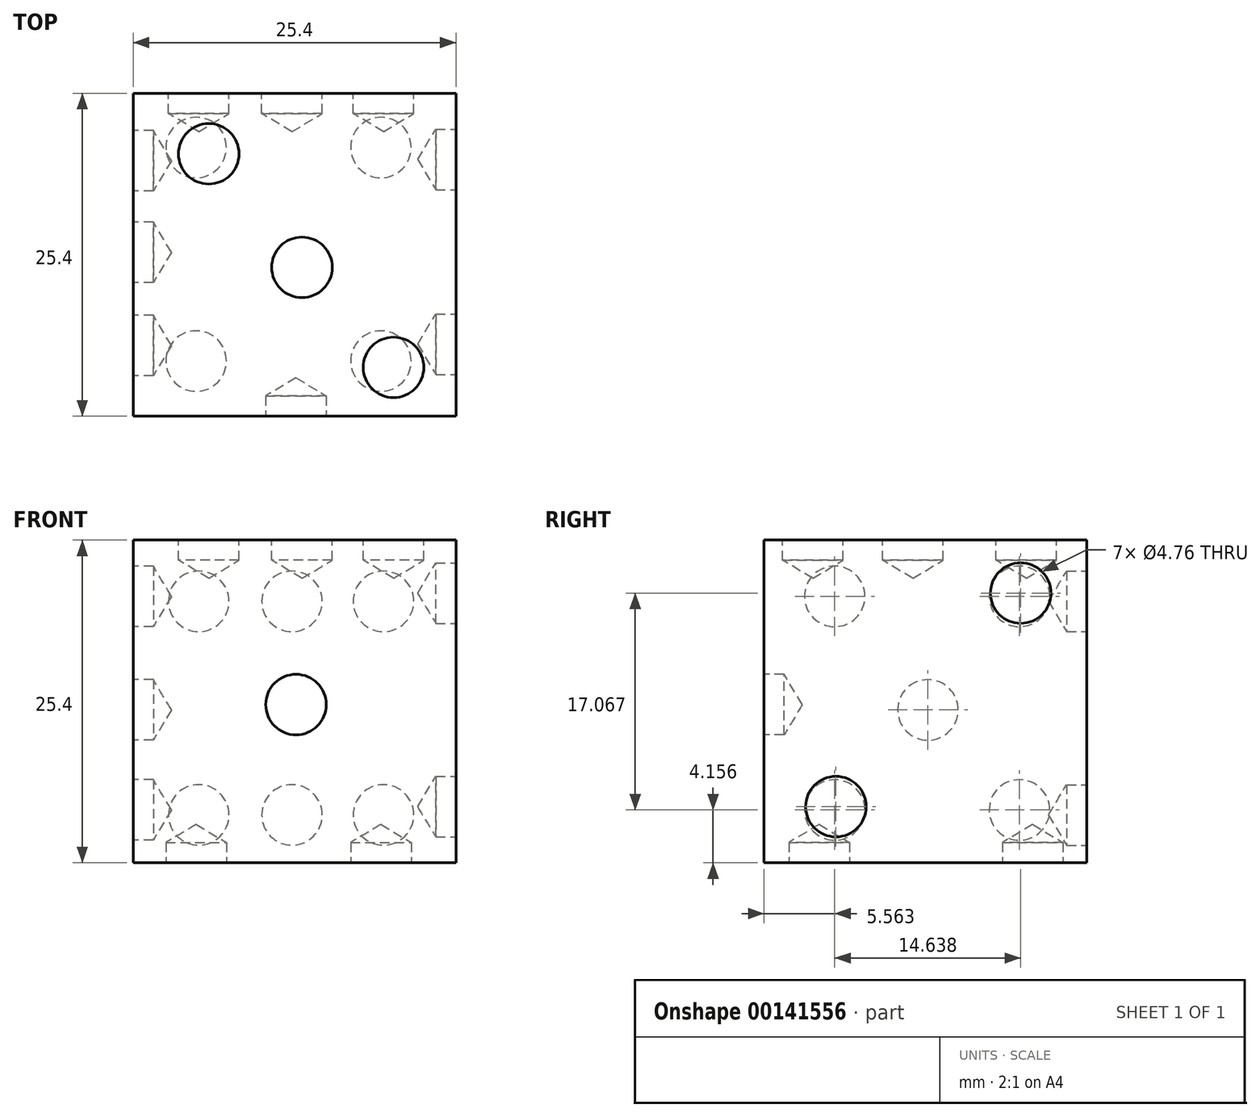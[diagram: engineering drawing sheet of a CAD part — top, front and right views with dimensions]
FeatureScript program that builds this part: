
annotation { "Feature Type Name" : "Feature", "Feature Type Description" : "" }
export const myFeature = defineFeature(function(context is Context, id is Id, definition is map)
    precondition{}
    {
        {
            var Q0;
            Q0=qCreatedBy(makeId("Front.planeOp"),FACE);
            var sketch = newSketch(context, id + "F0", { "sketchPlane" : qUnion([Q0])});
            skLineSegment(sketch, "E0.bottom", {"start": v(0, 0) * mm, "end": v(25.4, 0) * mm});
            skLineSegment(sketch, "E0.top", {"start": v(0, 25.4) * mm, "end": v(25.4, 25.4) * mm});
            skLineSegment(sketch, "E0.left", {"start": v(0, 0) * mm, "end": v(0, 25.4) * mm});
            skLineSegment(sketch, "E0.right", {"start": v(25.4, 0) * mm, "end": v(25.4, 25.4) * mm});
            skSolve(sketch);
        }
        {
            var Q0;
            Q0 = qSketchRegion(id + "F0", true);
            extrude(context, id + "F1", {"entities" : qUnion([Q0]), "depth" : 25.4 * mm});
        }
        {
            var Q0;
            Q0=qCreatedBy(makeId("Front.planeOp"),FACE);
            var sketch = newSketch(context, id + "F2", { "sketchPlane" : qUnion([Q0])});
            skPoint(sketch, "E1", {"position": v(5.16, 3.76) * mm});
            skPoint(sketch, "E2", {"position": v(12.5, 3.76) * mm});
            skPoint(sketch, "E3", {"position": v(19.7, 3.76) * mm});
            skPoint(sketch, "E4", {"position": v(19.7, 20.57) * mm});
            skPoint(sketch, "E5", {"position": v(12.5, 20.57) * mm});
            skPoint(sketch, "E6", {"position": v(5.16, 20.57) * mm});
            skSolve(sketch);
        }
        {
            var Q0;
            Q0=qCreatedBy(makeId("Right.planeOp"),FACE);
            var sketch = newSketch(context, id + "F3", { "sketchPlane" : qUnion([Q0])});
            skPoint(sketch, "E7", {"position": v(-19.84, 4.16) * mm});
            skPoint(sketch, "E8", {"position": v(-5.3, 4.16) * mm});
            skPoint(sketch, "E9", {"position": v(-5.3, 20.96) * mm});
            skPoint(sketch, "E10", {"position": v(-12.5, 12.03) * mm});
            skPoint(sketch, "E11", {"position": v(-19.84, 20.96) * mm});
            skSolve(sketch);
        }
        {
            var Q0;
            Q0=qCreatedBy(makeId("Top.planeOp"),FACE);
            var sketch = newSketch(context, id + "F4", { "sketchPlane" : qUnion([Q0])});
            skPoint(sketch, "E12", {"position": v(4.96, -21.06) * mm});
            skPoint(sketch, "E13", {"position": v(19.5, -21.06) * mm});
            skPoint(sketch, "E14", {"position": v(19.5, -4.26) * mm});
            skPoint(sketch, "E15", {"position": v(4.96, -4.26) * mm});
            skSolve(sketch);
        }
        {
            var Q0;
            Q0=sQuery(id+"F2.wireOp",VERTEX,"E6");
            var Q1;
            Q1=sQuery(id+"F2.wireOp",VERTEX,"E5");
            var Q2;
            Q2=sQuery(id+"F2.wireOp",VERTEX,"E4");
            var Q3;
            Q3=sQuery(id+"F2.wireOp",VERTEX,"E1");
            var Q4;
            Q4=sQuery(id+"F4.wireOp",VERTEX,"E12");
            var Q5;
            Q5=sQuery(id+"F2.wireOp",VERTEX,"E2");
            var Q6;
            Q6=sQuery(id+"F2.wireOp",VERTEX,"E3");
            var Q7;
            Q7=sQuery(id+"F4.wireOp",VERTEX,"E13");
            var Q8;
            Q8=sQuery(id+"F3.wireOp",VERTEX,"E9");
            var Q9;
            Q9=sQuery(id+"F3.wireOp",VERTEX,"E10");
            var Q10;
            Q10=sQuery(id+"F3.wireOp",VERTEX,"E7");
            var Q11;
            Q11=sQuery(id+"F3.wireOp",VERTEX,"E11");
            var Q12;
            Q12=sQuery(id+"F3.wireOp",VERTEX,"E8");
            var Q13;
            Q13=sQuery(id+"F4.wireOp",VERTEX,"E15");
            var Q14;
            Q14=sQuery(id+"F4.wireOp",VERTEX,"E14");
            var Q15;
            Q15=makeQuery(id+"F1.opExtrude","SWEPT_BODY",BODY,{"disambiguationData":[OSD([sQuery(id+"F0.wireOp",EDGE,"E0.bottom"),sQuery(id+"F0.wireOp",EDGE,"E0.top"),sQuery(id+"F0.wireOp",EDGE,"E0.left"),sQuery(id+"F0.wireOp",EDGE,"E0.right")])]});
            hole(context, id + "F5", {"style" : HoleStyle.SIMPLE, "endStyle" : HoleEndStyle.BLIND, "oppositeDirection" : true, "holeDiameter" : 4.76 * mm, "holeDepth" : 1.59 * mm, "locations" : qUnion([Q0, Q1, Q2, Q3, Q4, Q5, Q6, Q7, Q8, Q9, Q10, Q11, Q12, Q13, Q14]), "scope" : qUnion([Q15])});
        }
        {
            var Q0;
            Q0=qCreatedBy(makeId("Right.planeOp"),FACE);
            cPlane(context, id + "F6", {"entities" : qUnion([Q0]), "cplaneType" : CPlaneType.OFFSET, "offset" : 25.4 * mm, "width" : 152.4 * mm, "height" : 152.4 * mm});
        }
        {
            var Q0;
            Q0=qCreatedBy(id+"F6.planeOp",FACE);
            var sketch = newSketch(context, id + "F7", { "sketchPlane" : qUnion([Q0])});
            skPoint(sketch, "E16", {"position": v(-19.74, 4.42) * mm});
            skPoint(sketch, "E17", {"position": v(-5.2, 21.22) * mm});
            skSolve(sketch);
        }
        {
            var Q0;
            Q0=qCreatedBy(makeId("Front.planeOp"),FACE);
            cPlane(context, id + "F8", {"entities" : qUnion([Q0]), "cplaneType" : CPlaneType.OFFSET, "offset" : 25.4 * mm, "width" : 152.4 * mm, "height" : 152.4 * mm});
        }
        {
            var Q0;
            Q0=qCreatedBy(id+"F8.planeOp",FACE);
            var sketch = newSketch(context, id + "F9", { "sketchPlane" : qUnion([Q0])});
            skPoint(sketch, "E18", {"position": v(12.82, 12.45) * mm});
            skSolve(sketch);
        }
        {
            var Q0;
            Q0=qCreatedBy(makeId("Top.planeOp"),FACE);
            cPlane(context, id + "F10", {"entities" : qUnion([Q0]), "cplaneType" : CPlaneType.OFFSET, "offset" : 25.4 * mm, "width" : 152.4 * mm, "height" : 152.4 * mm});
        }
        {
            var Q0;
            Q0=qCreatedBy(id+"F10.planeOp",FACE);
            var sketch = newSketch(context, id + "F11", { "sketchPlane" : qUnion([Q0])});
            skPoint(sketch, "E19", {"position": v(20.49, -21.56) * mm});
            skPoint(sketch, "E20", {"position": v(13.29, -13.7) * mm});
            skPoint(sketch, "E21", {"position": v(5.95, -4.76) * mm});
            skSolve(sketch);
        }
        {
            var Q0;
            Q0=sQuery(id+"F11.wireOp",VERTEX,"E21");
            var Q1;
            Q1=sQuery(id+"F11.wireOp",VERTEX,"E20");
            var Q2;
            Q2=sQuery(id+"F9.wireOp",VERTEX,"E18");
            var Q3;
            Q3=sQuery(id+"F11.wireOp",VERTEX,"E19");
            var Q4;
            Q4=sQuery(id+"F7.wireOp",VERTEX,"E16");
            var Q5;
            Q5=sQuery(id+"F7.wireOp",VERTEX,"E17");
            var Q6;
            Q6=makeQuery(id+"F1.opExtrude","SWEPT_BODY",BODY,{"disambiguationData":[OSD([sQuery(id+"F0.wireOp",EDGE,"E0.bottom"),sQuery(id+"F0.wireOp",EDGE,"E0.top"),sQuery(id+"F0.wireOp",EDGE,"E0.left"),sQuery(id+"F0.wireOp",EDGE,"E0.right")])]});
            hole(context, id + "F12", {"style" : HoleStyle.SIMPLE, "endStyle" : HoleEndStyle.BLIND, "holeDiameter" : 4.76 * mm, "holeDepth" : 1.59 * mm, "locations" : qUnion([Q0, Q1, Q2, Q3, Q4, Q5]), "scope" : qUnion([Q6])});
        }
    });
